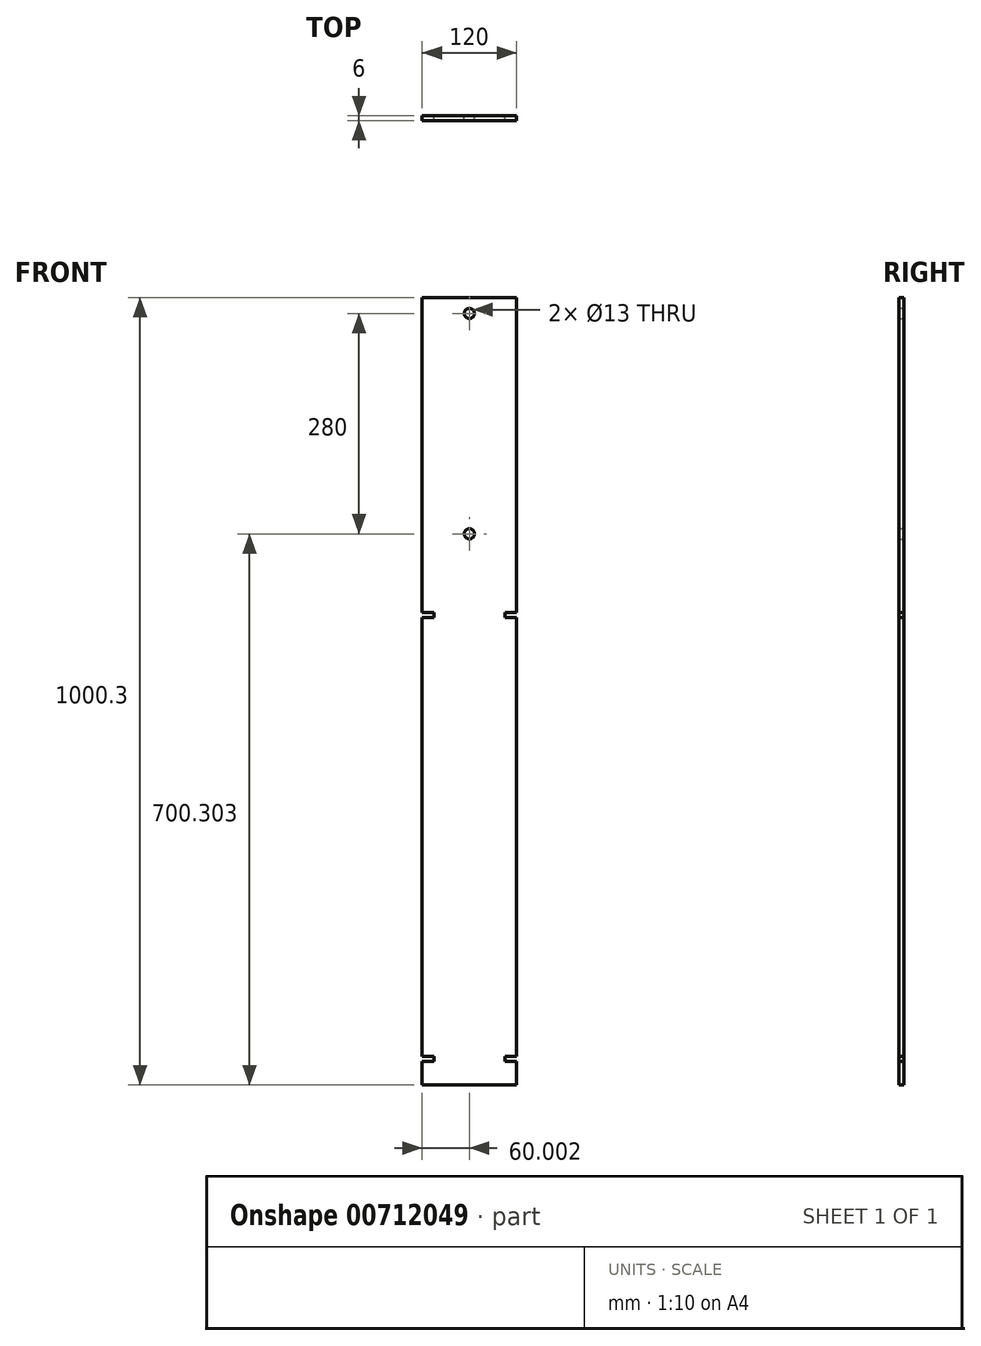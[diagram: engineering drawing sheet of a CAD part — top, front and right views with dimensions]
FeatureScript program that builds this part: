
annotation { "Feature Type Name" : "Feature", "Feature Type Description" : "" }
export const myFeature = defineFeature(function(context is Context, id is Id, definition is map)
    precondition{}
    {
        {
            var Q0;
            Q0=qCreatedBy(makeId("Front.planeOp"),FACE);
            var sketch = newSketch(context, id + "F0", { "sketchPlane" : qUnion([Q0])});
            skLineSegment(sketch, "E0", {"start": v(-86.23, 925.18) * mm, "end": v(-86.23, 525.18) * mm});
            skLineSegment(sketch, "E1", {"start": v(-86.23, 525.18) * mm, "end": v(-71.23, 525.18) * mm});
            skLineSegment(sketch, "E2", {"start": v(-71.23, 525.18) * mm, "end": v(-71.23, 518.68) * mm});
            skLineSegment(sketch, "E3", {"start": v(-71.23, 518.68) * mm, "end": v(-86.23, 518.68) * mm});
            skLineSegment(sketch, "E4", {"start": v(-86.23, 518.68) * mm, "end": v(-86.23, -38.62) * mm});
            skLineSegment(sketch, "E5", {"start": v(-86.23, -38.62) * mm, "end": v(-71.23, -38.62) * mm});
            skLineSegment(sketch, "E6", {"start": v(-71.23, -38.62) * mm, "end": v(-71.23, -45.12) * mm});
            skLineSegment(sketch, "E7", {"start": v(-71.23, -45.12) * mm, "end": v(-86.23, -45.12) * mm});
            skLineSegment(sketch, "E8", {"start": v(-86.23, -45.12) * mm, "end": v(-86.23, -75.12) * mm});
            skLineSegment(sketch, "E9", {"start": v(-86.23, -75.12) * mm, "end": v(33.77, -75.12) * mm});
            skLineSegment(sketch, "E10.MirrorCS", {"start": v(18.77, -45.12) * mm, "end": v(33.77, -45.12) * mm});
            skLineSegment(sketch, "E11.MirrorCS", {"start": v(18.77, -38.62) * mm, "end": v(18.77, -45.12) * mm});
            skLineSegment(sketch, "E12.MirrorCS", {"start": v(18.77, 525.18) * mm, "end": v(18.77, 518.68) * mm});
            skLineSegment(sketch, "E13.MirrorCS", {"start": v(33.77, 525.18) * mm, "end": v(18.77, 525.18) * mm});
            skLineSegment(sketch, "E14.MirrorCS", {"start": v(33.77, -38.62) * mm, "end": v(18.77, -38.62) * mm});
            skLineSegment(sketch, "E15.MirrorCS", {"start": v(18.77, 518.68) * mm, "end": v(33.77, 518.68) * mm});
            skLineSegment(sketch, "E16.MirrorCS", {"start": v(33.77, -45.12) * mm, "end": v(33.77, -75.12) * mm});
            skLineSegment(sketch, "E17.MirrorCS", {"start": v(33.77, 925.18) * mm, "end": v(33.77, 525.18) * mm});
            skLineSegment(sketch, "E18.MirrorCS", {"start": v(33.77, 518.68) * mm, "end": v(33.77, -38.62) * mm});
            skLineSegment(sketch, "E19", {"start": v(-86.23, 925.18) * mm, "end": v(33.77, 925.18) * mm});
            skCircle(sketch, "E20", {"center": v(-26.23, 905.18) * mm, "radius": 6.5 * mm});
            skPoint(sketch, "E20.centerSnap0", {"position": v(-26.23, 925.18) * mm});
            skCircle(sketch, "E21", {"center": v(-26.23, 625.18) * mm, "radius": 6.5 * mm});
            skSolve(sketch);
        }
        {
            var Q0;
            Q0=makeQuery(id+"F0.imprint","IMPRINT",FACE,{"disambiguationData":[TD([[makeQuery(id+"F0.imprint","IMPRINT",EDGE,{"derivedFrom":sQuery(id+"F0.wireOp",EDGE,"E0")}),1.0]])]});
            extrude(context, id + "F1", {"entities" : qUnion([Q0]), "depth" : 6 * mm, "offsetDistance" : 25 * mm});
        }
    });
